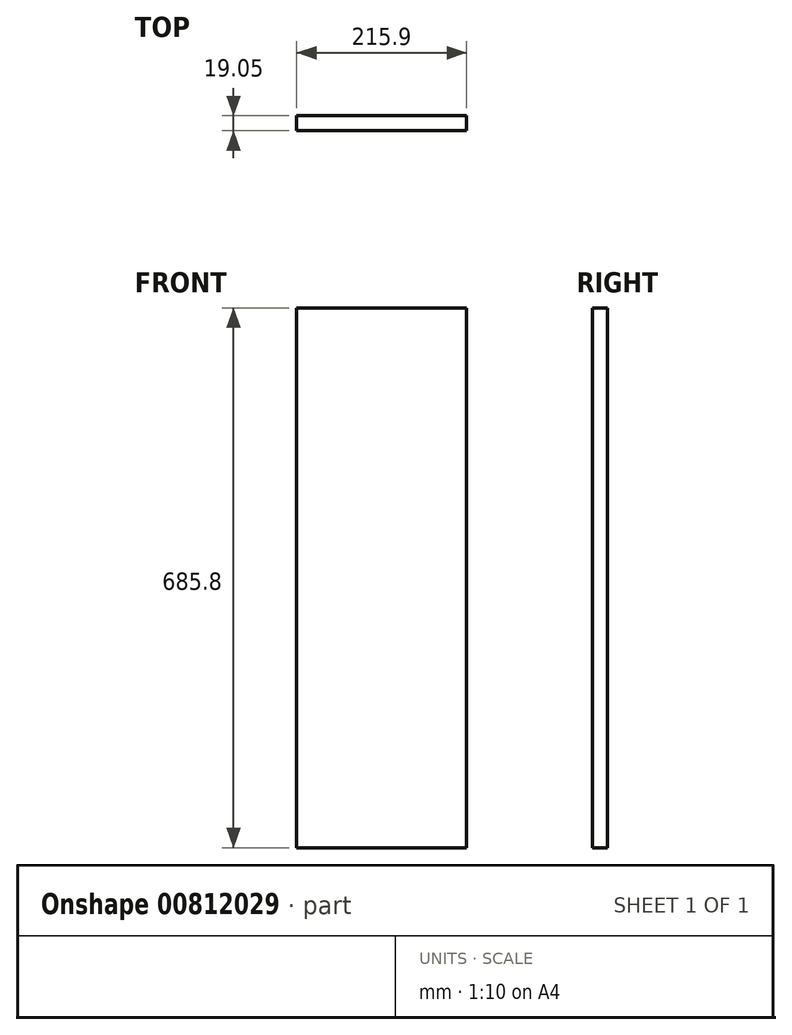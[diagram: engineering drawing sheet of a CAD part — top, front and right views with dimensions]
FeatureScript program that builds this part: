
annotation { "Feature Type Name" : "Feature", "Feature Type Description" : "" }
export const myFeature = defineFeature(function(context is Context, id is Id, definition is map)
    precondition{}
    {
        {
            var Q0;
            Q0=qCreatedBy(makeId("Front.planeOp"),FACE);
            var sketch = newSketch(context, id + "F0", { "sketchPlane" : qUnion([Q0])});
            skLineSegment(sketch, "E0.bottom", {"start": v(107.95, 342.9) * mm, "end": v(-107.95, 342.9) * mm});
            skLineSegment(sketch, "E0.top", {"start": v(107.95, -342.9) * mm, "end": v(-107.95, -342.9) * mm});
            skLineSegment(sketch, "E0.left", {"start": v(107.95, 342.9) * mm, "end": v(107.95, -342.9) * mm});
            skLineSegment(sketch, "E0.right", {"start": v(-107.95, 342.9) * mm, "end": v(-107.95, -342.9) * mm});
            skPoint(sketch, "E0.middle", {"position": v(0, 0) * mm});
            skSolve(sketch);
        }
        {
            var Q0;
            Q0=makeQuery(id+"F0.imprint","IMPRINT",FACE,{"disambiguationData":[TD([[makeQuery(id+"F0.imprint","IMPRINT",EDGE,{"derivedFrom":sQuery(id+"F0.wireOp",EDGE,"E0.bottom")}),1.0]])]});
            extrude(context, id + "F1", {"entities" : qUnion([Q0]), "depth" : 19.05 * mm, "offsetDistance" : 25.4 * mm});
        }
    });
